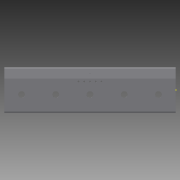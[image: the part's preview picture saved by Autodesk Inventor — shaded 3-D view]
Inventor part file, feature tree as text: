
AUTODESK INVENTOR PART (.ipt)
format: ipt  version: 2015 (Build 190159000, 159)  size: 340,480 bytes
history: native  units: mm
features: hole x21, sketch x7, other x7, sheet_metal_op x3
ambient origin geometry x8: Origin, YZ Plane, XZ Plane, XY Plane, X Axis, Y Axis, Z Axis, Center Point
bodies: Solid1 (feature_tree)
feature tree (38):
  sheet_metal_op  "Contour Flange1"
  sketch  "Sketch7"  dims[d20=0.5mm d21=6.0mm d22=1.5mm d23=1.5mm d24=1.5mm d25=0.0mm d26=1.5mm d27=0.0mm d28=1.5mm d29=0.0mm d30=1.5mm d31=0.0mm d32=17.0mm d33=8.0mm d34=2.5mm d35=6.0mm d36=4.0mm d37=2.0mm d38=90.0deg d39=4.2mm d40=20.594885mm d41=17.0mm d42=8.0mm d43=2.5mm d44=6.0mm d45=4.0mm d46=2.0mm d47=90.0deg d48=4.2mm d49=20.594885mm d50=17.0mm d51=8.0mm d52=2.5mm d53=6.0mm d54=4.0mm d55=2.0mm d56=90.0deg d57=4.2mm d58=20.594885mm d59=17.0mm d60=8.0mm d61=2.5mm d62=6.0mm d63=4.0mm d64=2.0mm d65=90.0deg d66=4.2mm d67=20.594885mm d68=150.0mm d69=8.0mm d70=2.5mm d71=6.0mm d72=4.0mm d73=2.0mm d74=90.0deg d75=4.2mm d76=20.594885mm d77=150.0mm d78=8.0mm d79=2.5mm d80=6.0mm d81=4.0mm d82=2.0mm d83=90.0deg d84=4.2mm d85=20.594885mm d86=30.0mm d87=30.0mm d88=12.0mm d89=6.0mm d90=4.0mm d91=2.0mm d92=90.0deg d93=1.5mm d94=20.594885mm d95=30.0mm d96=90.0mm d97=12.0mm d98=6.0mm d99=4.0mm d100=2.0mm d101=90.0deg d102=1.5mm d103=20.594885mm d104=30.0mm d105=150.0mm d106=12.0mm d107=6.0mm d108=4.0mm d109=2.0mm d110=90.0deg d111=1.5mm d112=20.594885mm d113=30.0mm d114=30.0mm d115=12.0mm d116=6.0mm d117=4.0mm d118=2.0mm d119=90.0deg d120=1.5mm d121=20.594885mm d122=30.0mm d123=90.0mm d124=12.0mm d125=6.0mm d126=4.0mm d127=2.0mm d128=90.0deg d129=1.5mm d130=20.594885mm d131=30.0mm d132=10.0mm d133=3.0mm d134=6.0mm d135=4.0mm d136=2.0mm d137=90.0deg d138=1.5mm d139=20.594885mm d140=10.0mm d141=90.0mm d142=3.0mm d143=6.0mm d144=4.0mm d145=2.0mm d146=90.0deg d147=1.5mm d148=20.594885mm d149=10.0mm d150=150.0mm d151=3.0mm d152=6.0mm d153=4.0mm d154=2.0mm d155=90.0deg d156=1.5mm d157=20.594885mm d158=10.0mm d159=90.0mm d160=3.0mm d161=6.0mm d162=4.0mm d163=2.0mm d164=90.0deg d165=1.5mm d166=20.594885mm d167=10.0mm d168=30.0mm d169=3.0mm d170=6.0mm d171=4.0mm d172=2.0mm d173=90.0deg d174=1.5mm d175=20.594885mm d181=130.0mm d182=5.0mm d183=3.0mm d184=6.0mm d185=4.0mm d186=2.0mm d187=90.0deg d188=1.5mm d189=20.594885mm d190=140.0mm d191=5.0mm d192=3.0mm d193=6.0mm d194=4.0mm d195=2.0mm d196=90.0deg d197=1.5mm d198=20.594885mm d199=150.0mm d200=5.0mm d201=3.0mm d202=6.0mm d203=4.0mm d204=2.0mm d205=90.0deg d206=1.5mm d207=20.594885mm d208=140.0mm d209=5.0mm d210=3.0mm d211=6.0mm d212=4.0mm d213=2.0mm d214=90.0deg d215=1.5mm d216=20.594885mm d217=130.0mm d218=5.0mm d219=3.0mm d220=6.0mm d221=4.0mm d222=2.0mm d223=90.0deg d224=1.5mm d225=20.594885mm d0=1.5mm d1=0.0mm d2=1.5mm d3=0.0mm d4=1.5mm d5=0.0mm d6=1.5mm d7=0.0mm d178=1.0mm d179=1.0mm]
  other  "A-Side Definition"
  hole  "Hole1"  [1 undecoded]
  hole  "Hole2"  [1 undecoded]
  hole  "Hole3"  [1 undecoded]
  hole  "Hole4"  [1 undecoded]
  hole  "Hole5"  [1 undecoded]
  hole  "Hole6"  [1 undecoded]
  hole  "Hole7"  [1 undecoded]
  hole  "Hole8"  [1 undecoded]
  hole  "Hole9"  [1 undecoded]
  hole  "Hole10"  [1 undecoded]
  hole  "Hole11"  [1 undecoded]
  hole  "Hole12"  [1 undecoded]
  hole  "Hole13"  [1 undecoded]
  hole  "Hole14"  [1 undecoded]
  hole  "Hole15"  [1 undecoded]
  hole  "Hole16"  [1 undecoded]
  hole  "Hole17"  [1 undecoded]
  hole  "Hole18"  [1 undecoded]
  hole  "Hole19"  [1 undecoded]
  hole  "Hole20"  [1 undecoded]
  hole  "Hole21"  [1 undecoded]
  sketch  "Sketch1"  dims[d8=25.0mm d9=35.0mm]
  other  "Plate1"
  sheet_metal_op  "Bend1"
  sheet_metal_op  "Corner1"
  sketch  "Sketch3"  dims[d12=20.0mm d13=20.0mm]
  sketch  "Sketch4"  dims[d14=1.5mm d15=0.75mm]
  sketch  "Sketch5"  dims[d16=3.0mm d17=1.5mm]
  sketch  "Sketch6"  dims[d18=300.0mm d19=1.5mm]
  other  "Cut1"
  other  "Cut2"
  other  "Cut3"
  other  "Cut4"
  other  "Definition1"
  sketch  "Sketch2"  dims[d10=20.0mm d11=10.0mm]
note: 21 required parameter values undecoded (feature->parameter linkage not recoverable at this tier; creation-order binding heuristic only, values carry confidence <= 0.55)
